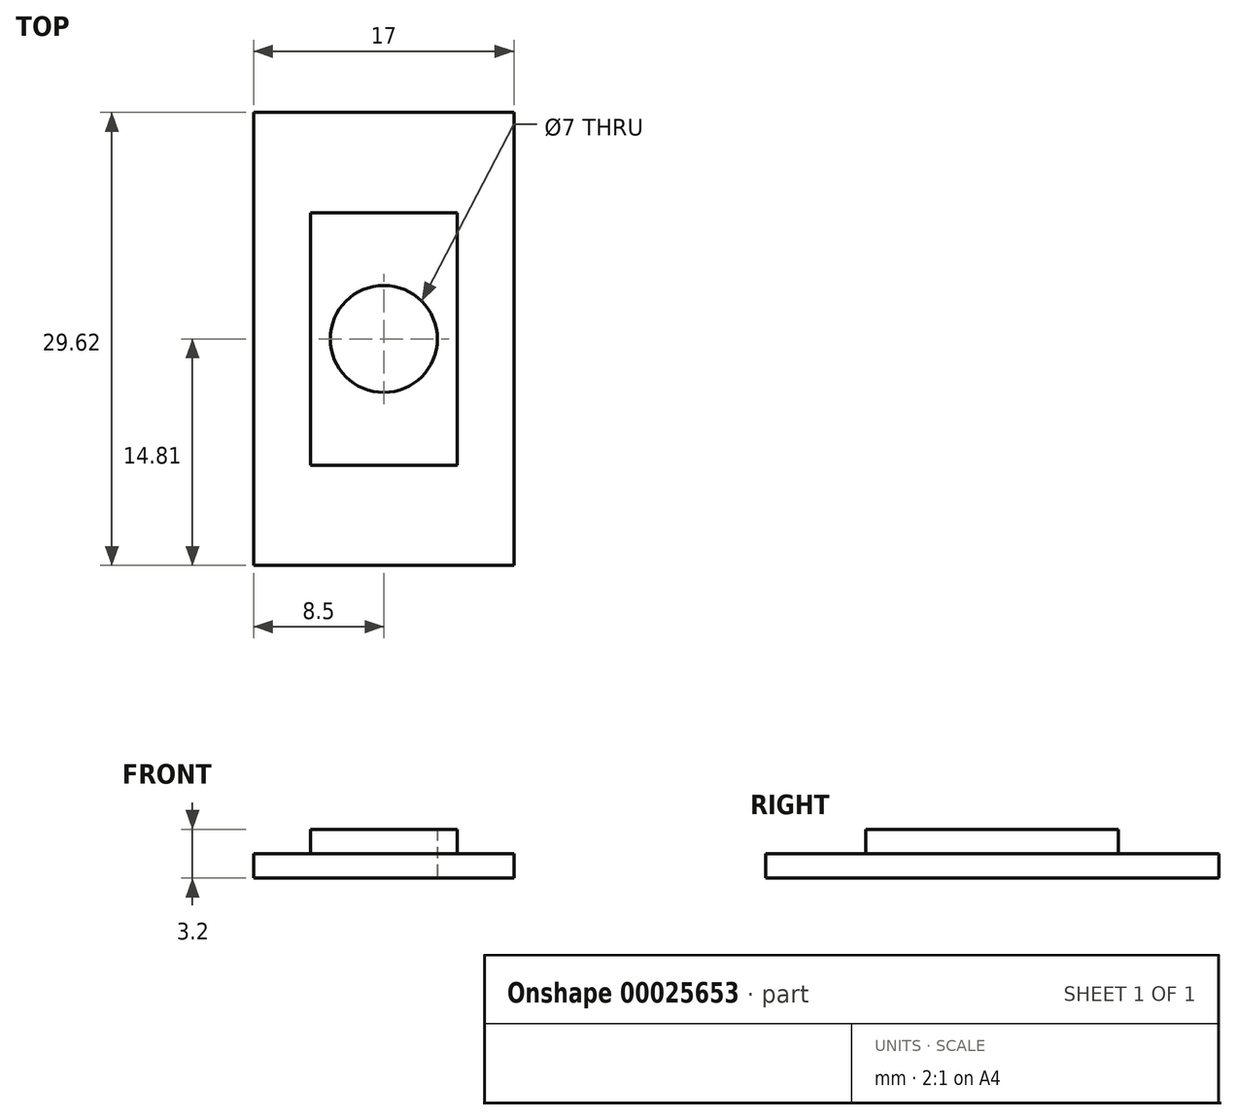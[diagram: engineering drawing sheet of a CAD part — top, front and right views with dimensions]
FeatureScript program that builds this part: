
annotation { "Feature Type Name" : "Feature", "Feature Type Description" : "" }
export const myFeature = defineFeature(function(context is Context, id is Id, definition is map)
    precondition{}
    {
        {
            var Q0;
            Q0=qCreatedBy(makeId("Top.planeOp"),FACE);
            var sketch = newSketch(context, id + "F0", { "sketchPlane" : qUnion([Q0])});
            skLineSegment(sketch, "E0.rect.bottom", {"start": v(4.8, -8.25) * mm, "end": v(-4.8, -8.25) * mm});
            skLineSegment(sketch, "E0.rect.top", {"start": v(4.8, 8.25) * mm, "end": v(-4.8, 8.25) * mm});
            skLineSegment(sketch, "E0.rect.left", {"start": v(4.8, -8.25) * mm, "end": v(4.8, 8.25) * mm});
            skLineSegment(sketch, "E0.rect.right", {"start": v(-4.8, -8.25) * mm, "end": v(-4.8, 8.25) * mm});
            skPoint(sketch, "E0.rect.middle", {"position": v(0, 0) * mm});
            skCircle(sketch, "E1", {"center": v(0, 0) * mm, "radius": 3.5 * mm});
            skSolve(sketch);
        }
        {
            var Q0;
            Q0 = qSketchRegion(id + "F0", true);
            extrude(context, id + "F1", {"entities" : qUnion([Q0]), "depth" : 1.6 * mm});
        }
        {
            var Q0;
            Q0=qCreatedBy(makeId("Top.planeOp"),FACE);
            var sketch = newSketch(context, id + "F2", { "sketchPlane" : qUnion([Q0])});
            skLineSegment(sketch, "E2.rect.bottom", {"start": v(8.5, -14.81) * mm, "end": v(-8.5, -14.81) * mm});
            skLineSegment(sketch, "E2.rect.top", {"start": v(8.5, 14.81) * mm, "end": v(-8.5, 14.81) * mm});
            skLineSegment(sketch, "E2.rect.left", {"start": v(8.5, -14.81) * mm, "end": v(8.5, 14.81) * mm});
            skLineSegment(sketch, "E2.rect.right", {"start": v(-8.5, -14.81) * mm, "end": v(-8.5, 14.81) * mm});
            skPoint(sketch, "E2.rect.middle", {"position": v(0, 0) * mm});
            skCircle(sketch, "E3", {"center": v(0, 0) * mm, "radius": 3.5 * mm});
            skSolve(sketch);
        }
        {
            var Q0;
            Q0 = qSketchRegion(id + "F2", true);
            extrude(context, id + "F3", {"entities" : qUnion([Q0]), "operationType" : NewBodyOperationType.ADD, "oppositeDirection" : true, "depth" : 1.6 * mm});
        }
    });
